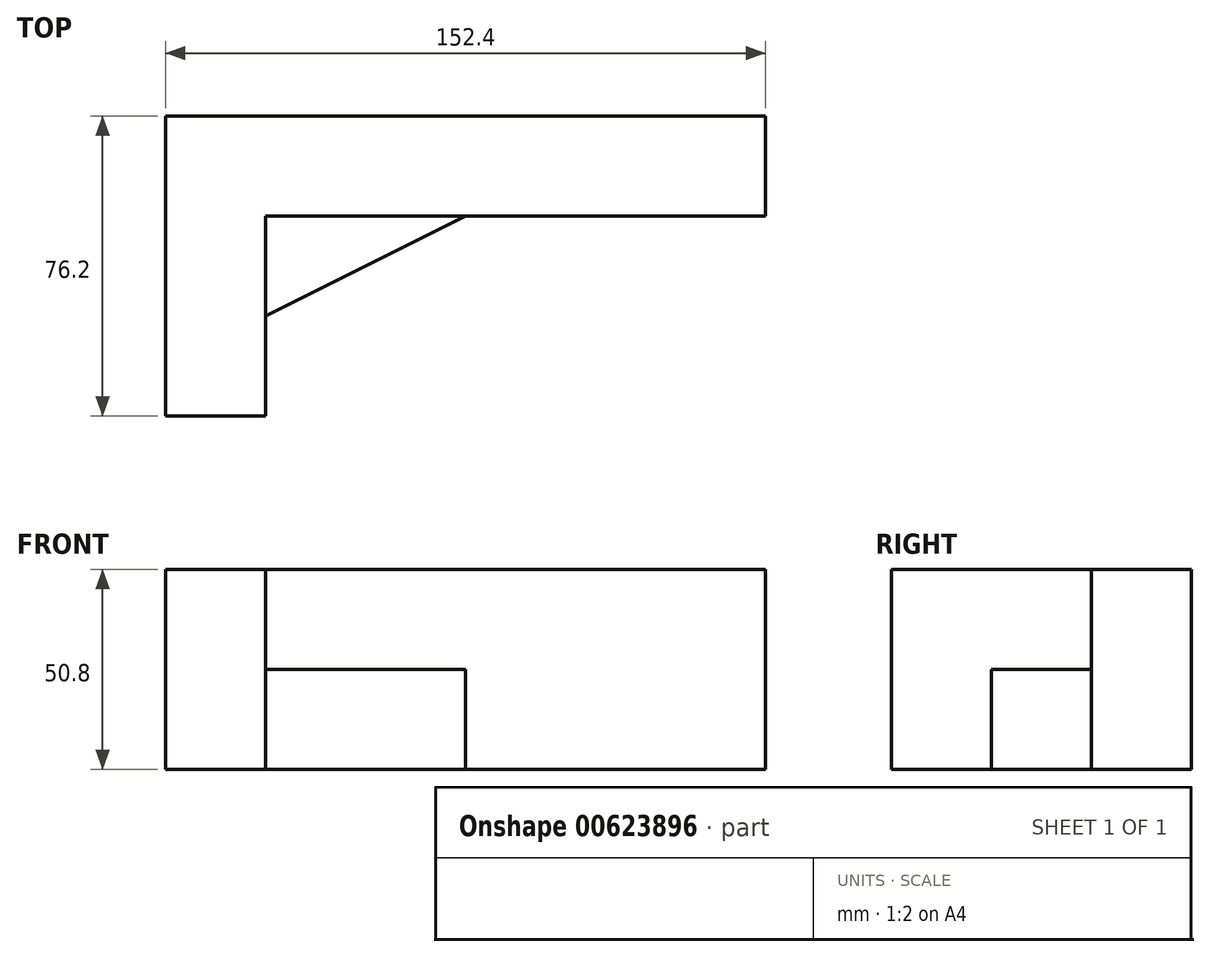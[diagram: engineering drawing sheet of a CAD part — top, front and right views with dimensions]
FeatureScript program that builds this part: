
annotation { "Feature Type Name" : "Feature", "Feature Type Description" : "" }
export const myFeature = defineFeature(function(context is Context, id is Id, definition is map)
    precondition{}
    {
        {
            var Q0;
            Q0=qCreatedBy(makeId("Front.planeOp"),FACE);
            var sketch = newSketch(context, id + "F0", { "sketchPlane" : qUnion([Q0])});
            skLineSegment(sketch, "E0.bottom", {"start": v(154.41, 0) * mm, "end": v(306.81, 0) * mm});
            skLineSegment(sketch, "E0.top", {"start": v(154.41, -50.8) * mm, "end": v(306.81, -50.8) * mm});
            skLineSegment(sketch, "E0.left", {"start": v(154.41, 0) * mm, "end": v(154.41, -50.8) * mm});
            skLineSegment(sketch, "E0.right", {"start": v(306.81, 0) * mm, "end": v(306.81, -50.8) * mm});
            skSolve(sketch);
        }
        {
            var Q0;
            Q0 = qSketchRegion(id + "F0", true);
            extrude(context, id + "F1", {"entities" : qUnion([Q0]), "depth" : 76.2 * mm, "offsetDistance" : 25.4 * mm});
        }
        {
            var Q0;
            Q0=makeQuery(id+"F1.opExtrude","CAP_FACE",FACE,{"disambiguationData":[OSD([sQuery(id+"F0.wireOp",EDGE,"E0.bottom"),sQuery(id+"F0.wireOp",EDGE,"E0.top"),sQuery(id+"F0.wireOp",EDGE,"E0.left"),sQuery(id+"F0.wireOp",EDGE,"E0.right")])],"isStart":false});
            var sketch = newSketch(context, id + "F2", { "sketchPlane" : qUnion([Q0])});
            skLineSegment(sketch, "E1.bottom", {"start": v(179.81, 0) * mm, "end": v(306.81, 0) * mm});
            skLineSegment(sketch, "E1.top", {"start": v(179.81, -50.8) * mm, "end": v(306.81, -50.8) * mm});
            skLineSegment(sketch, "E1.left", {"start": v(179.81, 0) * mm, "end": v(179.81, -50.8) * mm});
            skLineSegment(sketch, "E1.right", {"start": v(306.81, 0) * mm, "end": v(306.81, -50.8) * mm});
            skSolve(sketch);
        }
        {
            var Q0;
            Q0=makeQuery(id+"F2.imprint","IMPRINT",FACE,{"disambiguationData":[TD([[makeQuery(id+"F2.imprint","IMPRINT",EDGE,{"derivedFrom":sQuery(id+"F2.wireOp",EDGE,"E1.bottom")}),-1.0]])]});
            extrude(context, id + "F3", {"entities" : qUnion([Q0]), "operationType" : NewBodyOperationType.REMOVE, "oppositeDirection" : true, "depth" : 50.8 * mm, "offsetDistance" : 25.4 * mm});
        }
        {
            var Q0;
            Q0=makeQuery(id+"F3.boolean.opBoolean","COPY",FACE,{"derivedFrom":makeQuery(id+"F3.opExtrude","CAP_FACE",FACE,{"disambiguationData":[OSD([sQuery(id+"F2.wireOp",EDGE,"E1.bottom"),sQuery(id+"F2.wireOp",EDGE,"E1.top"),sQuery(id+"F2.wireOp",EDGE,"E1.left"),sQuery(id+"F2.wireOp",EDGE,"E1.right")])],"isStart":false})});
            var sketch = newSketch(context, id + "F4", { "sketchPlane" : qUnion([Q0])});
            skPoint(sketch, "E2.oppositeSnap0", {"position": v(179.81, -25.4) * mm});
            skLineSegment(sketch, "E2.bottom", {"start": v(179.81, -50.8) * mm, "end": v(230.61, -50.8) * mm});
            skLineSegment(sketch, "E2.top", {"start": v(179.81, -25.4) * mm, "end": v(230.61, -25.4) * mm});
            skLineSegment(sketch, "E2.left", {"start": v(179.81, -50.8) * mm, "end": v(179.81, -25.4) * mm});
            skLineSegment(sketch, "E2.right", {"start": v(230.61, -50.8) * mm, "end": v(230.61, -25.4) * mm});
            skSolve(sketch);
        }
        {
            var Q0;
            Q0=makeQuery(id+"F4.imprint","IMPRINT",FACE,{"disambiguationData":[TD([[makeQuery(id+"F4.imprint","IMPRINT",EDGE,{"derivedFrom":sQuery(id+"F4.wireOp",EDGE,"E2.bottom")}),1.0]])]});
            extrude(context, id + "F5", {"entities" : qUnion([Q0]), "operationType" : NewBodyOperationType.ADD, "depth" : 25.4 * mm, "offsetDistance" : 25.4 * mm});
        }
        {
            var Q0;
            Q0=makeQuery(id+"F5.opExtrude","SWEPT_FACE",FACE,{"disambiguationData":[OSD([sQuery(id+"F4.wireOp",EDGE,"E2.top")])]});
            var sketch = newSketch(context, id + "F6", { "sketchPlane" : qUnion([Q0])});
            skLineSegment(sketch, "E3", {"start": v(179.81, -50.8) * mm, "end": v(230.61, -25.4) * mm});
            skLineSegment(sketch, "E4", {"start": v(230.61, -25.4) * mm, "end": v(230.61, -50.8) * mm});
            skLineSegment(sketch, "E5", {"start": v(230.61, -50.8) * mm, "end": v(179.81, -50.8) * mm});
            skSolve(sketch);
        }
        {
            var Q0;
            Q0=makeQuery(id+"F6.imprint","IMPRINT",FACE,{"disambiguationData":[TD([[makeQuery(id+"F6.imprint","IMPRINT",EDGE,{"derivedFrom":sQuery(id+"F6.wireOp",EDGE,"E3")}),-1.0]])]});
            extrude(context, id + "F7", {"entities" : qUnion([Q0]), "operationType" : NewBodyOperationType.REMOVE, "oppositeDirection" : true, "depth" : 25.4 * mm, "offsetDistance" : 25.4 * mm});
        }
    });
